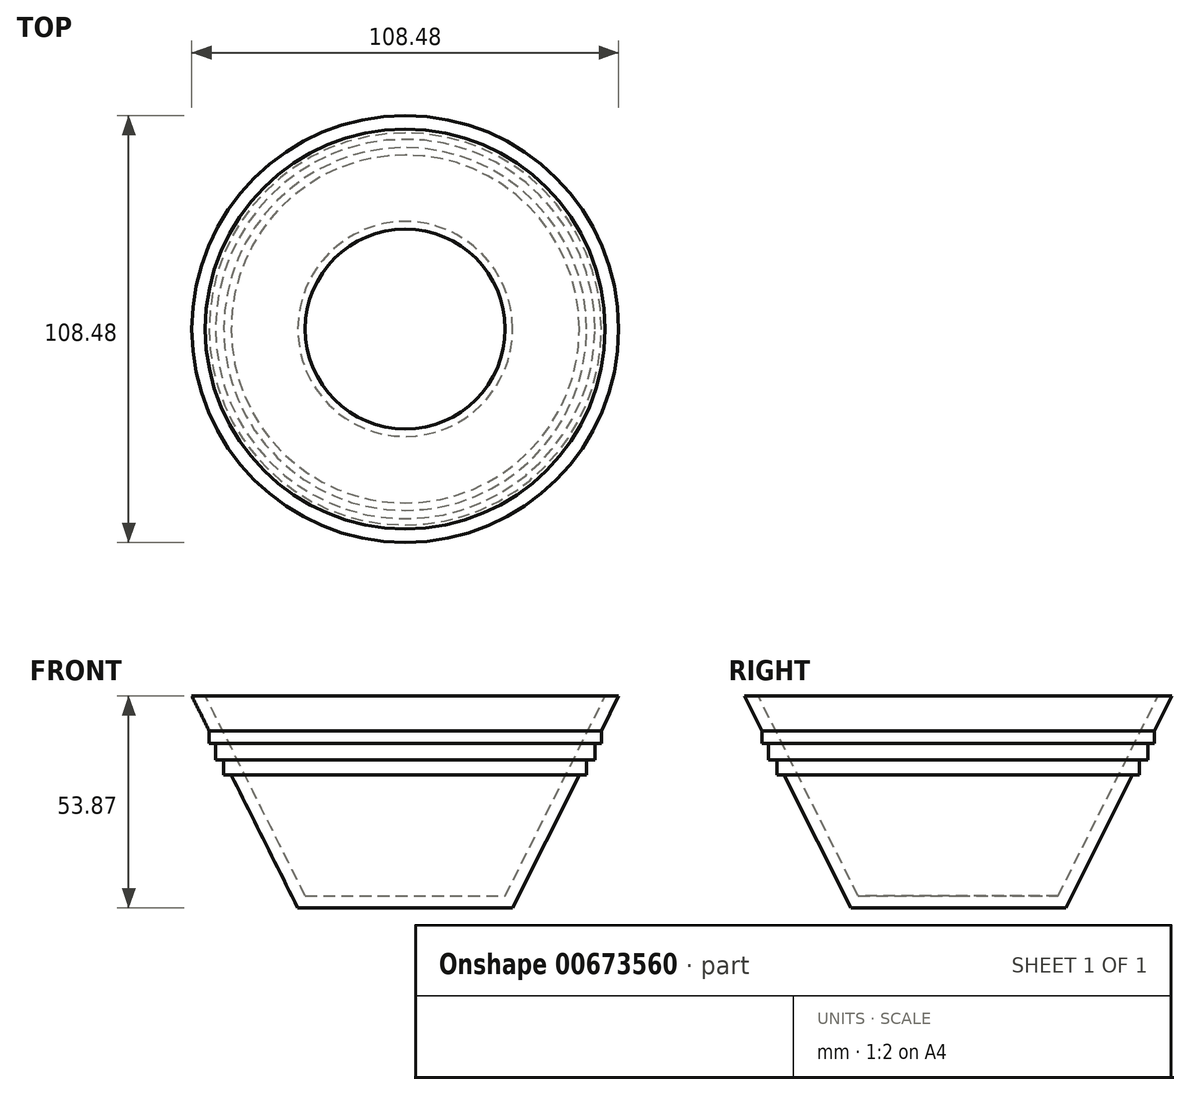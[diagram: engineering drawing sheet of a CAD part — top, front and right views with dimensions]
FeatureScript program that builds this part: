
annotation { "Feature Type Name" : "Feature", "Feature Type Description" : "" }
export const myFeature = defineFeature(function(context is Context, id is Id, definition is map)
    precondition{}
    {
        {
            var Q0;
            Q0=qCreatedBy(makeId("Front.planeOp"),FACE);
            var sketch = newSketch(context, id + "F0", { "sketchPlane" : qUnion([Q0])});
            skLineSegment(sketch, "E0", {"start": v(0, 0) * mm, "end": v(0, 50.8) * mm, "construction": true});
            skLineSegment(sketch, "E1", {"start": v(0, 0) * mm, "end": v(25.4, 0) * mm});
            skLineSegment(sketch, "E2", {"start": v(25.4, 0) * mm, "end": v(50.8, 50.8) * mm});
            skLineSegment(sketch, "E3.0", {"start": v(27.3, -3.07) * mm, "end": v(54.24, 50.8) * mm});
            skLineSegment(sketch, "E3.1", {"start": v(0, -3.07) * mm, "end": v(27.3, -3.07) * mm});
            skLineSegment(sketch, "E4", {"start": v(0, 0) * mm, "end": v(0, -3.07) * mm});
            skLineSegment(sketch, "E5", {"start": v(54.24, 50.8) * mm, "end": v(50.8, 50.8) * mm});
            skLineSegment(sketch, "E6", {"start": v(49.82, 41.96) * mm, "end": v(49.82, 38.69) * mm});
            skLineSegment(sketch, "E7", {"start": v(49.82, 38.69) * mm, "end": v(48.18, 38.69) * mm});
            skLineSegment(sketch, "E8", {"start": v(48.18, 38.69) * mm, "end": v(48.18, 34.52) * mm});
            skLineSegment(sketch, "E9", {"start": v(48.18, 34.52) * mm, "end": v(46.1, 34.52) * mm});
            skLineSegment(sketch, "E10", {"start": v(46.1, 34.52) * mm, "end": v(46.1, 30.74) * mm});
            skLineSegment(sketch, "E11", {"start": v(46.1, 30.74) * mm, "end": v(44.2, 30.74) * mm});
            skSolve(sketch);
        }
        {
            var Q0;
            Q0=makeQuery(id+"F0.imprint","IMPRINT",FACE,{"disambiguationData":[TD([[makeQuery(id+"F0.imprint","IMPRINT",EDGE,{"derivedFrom":sQuery(id+"F0.wireOp",EDGE,"E1")}),-1.0]])]});
            var Q1;
            {var subQ0=sQuery(id+"F0.wireOp",EDGE,"E10");Q1=makeQuery(id+"F0.imprint","IMPRINT",FACE,{"disambiguationData":[TD([[makeQuery(id+"F0.imprint","IMPRINT",EDGE,{"derivedFrom":subQ0}),-1.0]])]});}
            var Q2;
            {var subQ0=sQuery(id+"F0.wireOp",EDGE,"E8");Q2=makeQuery(id+"F0.imprint","IMPRINT",FACE,{"disambiguationData":[TD([[makeQuery(id+"F0.imprint","IMPRINT",EDGE,{"derivedFrom":subQ0}),-1.0]])]});}
            var Q3;
            {var subQ0=sQuery(id+"F0.wireOp",EDGE,"E6");Q3=makeQuery(id+"F0.imprint","IMPRINT",FACE,{"disambiguationData":[TD([[makeQuery(id+"F0.imprint","IMPRINT",EDGE,{"derivedFrom":subQ0}),-1.0]])]});}
            var Q4;
            Q4=sQuery(id+"F0.wireOp",EDGE,"E0");
            revolve(context, id + "F1", {"entities" : qUnion([Q0, Q1, Q2, Q3]), "axis" : qUnion([Q4]), "revolveType" : RevolveType.FULL});
        }
    });
